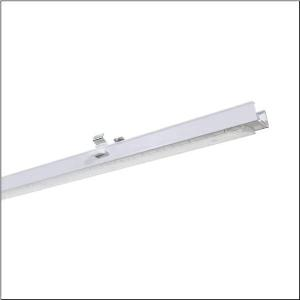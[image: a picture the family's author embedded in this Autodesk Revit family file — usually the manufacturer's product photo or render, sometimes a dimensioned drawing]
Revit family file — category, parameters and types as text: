
# Revit family: trunking_flex_31_51re14mb4cb
name_source: partatom
category: Lighting Fixtures
units: mm (PartAtom-declared; Revit-internal decimal feet)

## family parameters
Cut with Voids When Loaded = No
Host = Face
Light Source = No
Part Type = Normal
Room Calculation Point = No
Round Connector Dimension = Use Diameter
Shared = No

## types (1)
- --- (1 x LED, 11500 lm, 66 W, 4000K)
    Apparent Load = 66 VA
    CIE Flux Codes = 72 92 98 99 100
    Color Rendering = 80
    Color Temperature = 4000K
    Default Elevation = 1800 mm
    Description = Trunking Flex 31, luminaire insert, of extruded aluminium section, coated, traffic white (RAL 9016), length: 1.472mm, width: 91mm, height: 53mm, LED rated luminous flux: 11.500lm, light colour: 840, control gear: ON/OFF Multilumen, with system connector: socket, mains connection: 220..240V, AC, 50/60Hz, rated input power: 66W, connected load according to luminous flux setting (19/24/32/37/47/52/60/66W), luminous flux adjustable on luminaire in eight steps (3450/4380/5800/6700/8350/9200/10500/11500lm ), primary light control with lens, of plastic, primary optical cover: cover, of PMMA, light emission: direct distribution, primary light characteristic: asymmetric, protection rating (complete): IP20, insulation class (complete): insulation class I (protective earthing), certification: CE, UKCA, impact resistance: IK02, permissible ambient temperature for indoor applications: -20..+40°C, packaging unit: 1 piece
    Height = 58 mm
    Lamp = 1 x LED
    Lamp Light Flux = 11500 lm
    Lamp Power = 66 W
    Lamp count = 1
    Length = 1472 mm
    Luminous efficacy = 174 lm/W
    Manufacturer = Siteco
    ModVariant = No
    Model = 51RE14MB4CB
    Mounting Place = Ceiling
    Mounting Type = Pendant
    Number of Poles = 1
    OnlyDefault = Yes
    Power Factor = 1
    Product Name = Trunking Flex 31
    Product group = luminaire insert
    ProductGroupID = 901
    Protection Class = Protection class I
    Protection Degree = IP 20
    RLX_Detail_Level = 1
    RLX_Emergency_Light_Flux = 0 lm
    RLX_Emergency_Type = 0
    RLX_Emergency_Type_DB = No
    RlxData = <blob elided: 21677 chars, md5=f4b72dad>
    Socket = socket
    Standby Power = 0 W
    System Light Flux = 11500 lm
    System Power = 66 W
    Type Comments = factory setting: luminous flux: 100 % | (ON | ON | ON)
    Type Image = l_1266702.jpg
    URL = http://relux.com
    VarID = @adj_027219
    Voltage = 0 V
    Weight = 0.00 kg
    Width = 65 mm

## geometry (parser evidence)
native form markers: Blend x4, Sweep x10
no freeform markers — native parametric forms only
